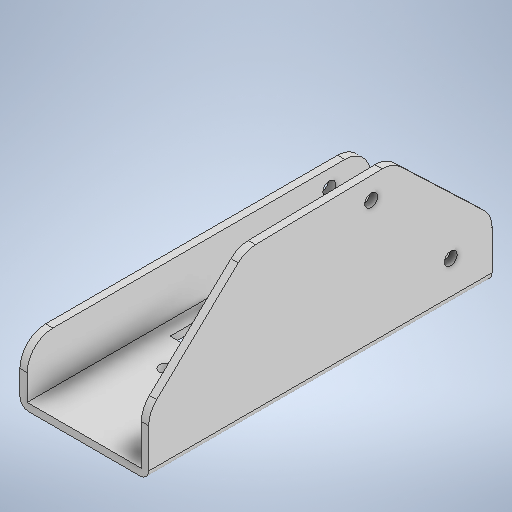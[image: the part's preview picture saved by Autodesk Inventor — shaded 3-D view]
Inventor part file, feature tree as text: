
AUTODESK INVENTOR PART (.ipt)
format: ipt  version: 2025.2 (Build 292293000, 293)  size: 311,296 bytes
history: native  units: mm
features: extrude x4, sketch x4, fillet x2
ambient origin geometry x8: Origin, YZ Plane, XZ Plane, XY Plane, X Axis, Y Axis, Z Axis, Center Point
bodies: Solid1 (feature_tree)
feature tree (10):
  extrude  "Extrusion1"  Depth=40.0mm
  extrude  "Extrusion2"  Depth=30.0mm
  extrude  "Extrusion3"  Depth=5.0mm
  fillet  "Fillet1"  Radius=1.7mm
  fillet  "Fillet2"  [1 undecoded]
  extrude  "Extrusion4"  Depth=6.0mm
  sketch  "Sketch1"  dims[d0=20.0mm d1=40.0mm]
  sketch  "Sketch2"  dims[d2=30.0mm d3=30.0mm]
  sketch  "Sketch3"  dims[d4=10.0mm d5=5.0mm d6=1.7mm d7=0.0mm d8=0.0mm]
  sketch  "Sketch4"  dims[d9=3.0mm d10=8.0mm d11=56.0mm d12=29.0mm d13=3.0mm d14=5.0mm d15=5.0mm d16=12.0mm d17=1.7mm d18=0.0mm d19=12.0mm d20=80.0mm d21=3.0mm d22=1.7mm d23=0.0mm d24=2.0mm d25=6.0mm d26=8.0mm d27=54.0mm d28=6.0mm d29=7.0mm d30=3.0mm d31=3.0mm d32=3.0mm d33=3.0mm d34=0.0mm d35=0.0mm]
note: 1 required parameter value undecoded (feature->parameter linkage not recoverable at this tier; creation-order binding heuristic only, values carry confidence <= 0.55)
